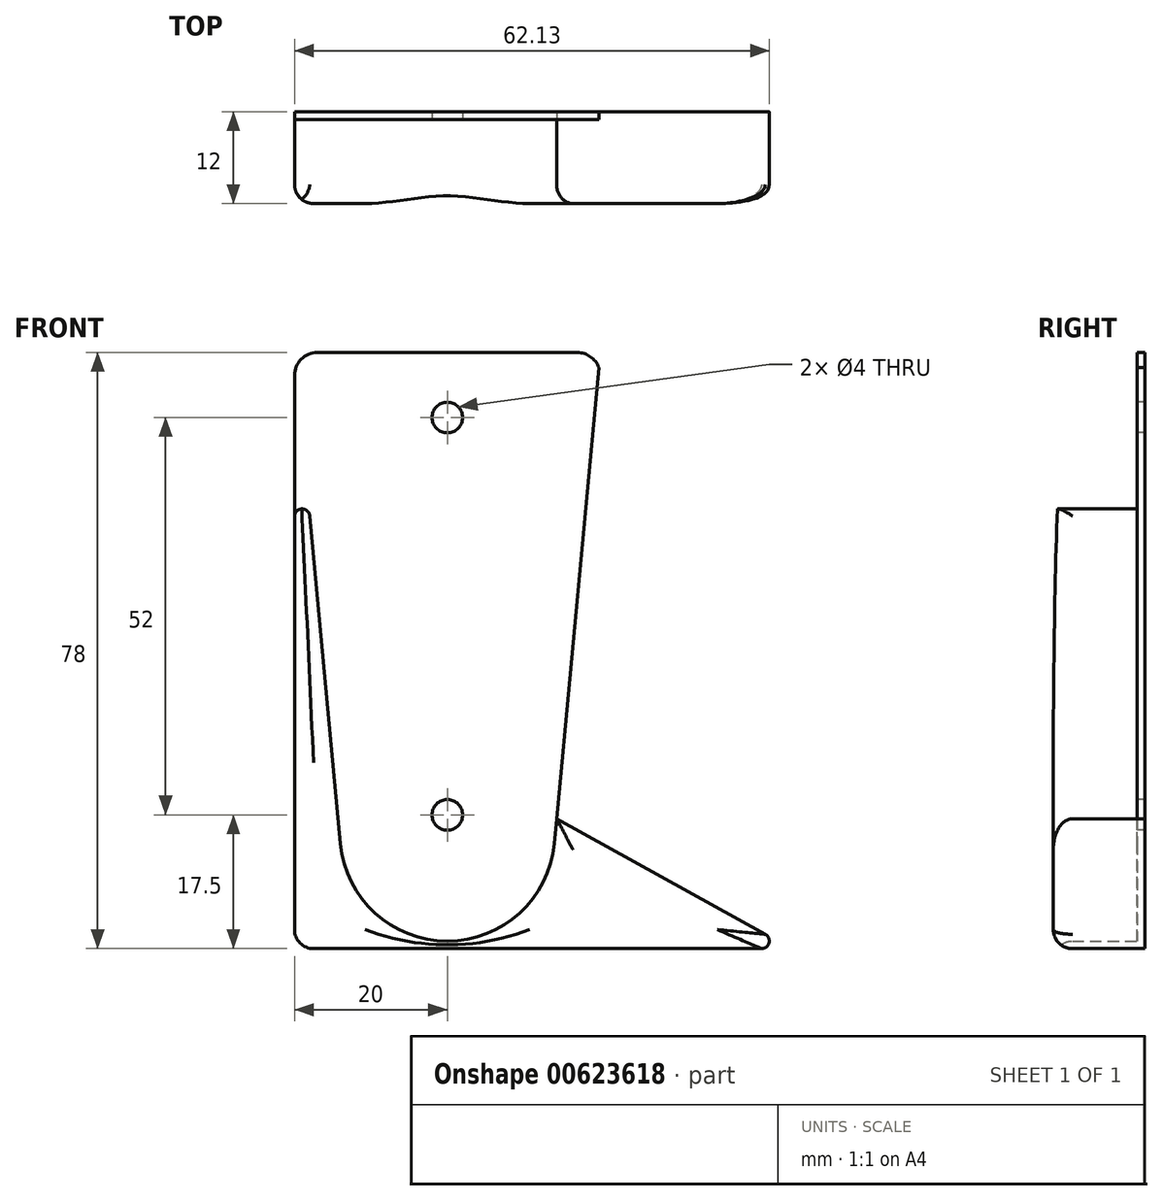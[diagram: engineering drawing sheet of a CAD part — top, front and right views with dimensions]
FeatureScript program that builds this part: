
annotation { "Feature Type Name" : "Feature", "Feature Type Description" : "" }
export const myFeature = defineFeature(function(context is Context, id is Id, definition is map)
    precondition{}
    {
        {
            var Q0;
            Q0=qCreatedBy(makeId("Front.planeOp"),FACE);
            var sketch = newSketch(context, id + "F0", { "sketchPlane" : qUnion([Q0])});
            skLineSegment(sketch, "E0.bottom", {"start": v(-20, 0) * mm, "end": v(20, 0) * mm});
            skLineSegment(sketch, "E0.top", {"start": v(-17, 78) * mm, "end": v(17, 78) * mm});
            skLineSegment(sketch, "E0.left", {"start": v(-20, 0) * mm, "end": v(-20, 75) * mm});
            skLineSegment(sketch, "E0.right", {"start": v(20, 0) * mm, "end": v(20, 75) * mm});
            skLineSegment(sketch, "E1", {"start": v(0, 78) * mm, "end": v(0, 0) * mm, "construction": true});
            skCircle(sketch, "E2", {"center": v(0, 69.5) * mm, "radius": 2 * mm});
            skCircle(sketch, "E3", {"center": v(0, 17.5) * mm, "radius": 2 * mm});
            skLineSegment(sketch, "E4", {"start": v(-12.72, 0) * mm, "end": v(-20, 78) * mm});
            skLineSegment(sketch, "E5", {"start": v(20, 0) * mm, "end": v(45, 0) * mm});
            skLineSegment(sketch, "E6", {"start": v(20, 78) * mm, "end": v(12.72, 0) * mm});
            skArc(sketch, "E7", {"start": v(-14, 13.75) * mm, "mid": v(0, 1) * mm, "end": v(14, 13.75) * mm});
            skLineSegment(sketch, "E8", {"start": v(45, 0) * mm, "end": v(14.3, 17) * mm});
            skPoint(sketch, "E9.visualSharp", {"position": v(20, 78) * mm});
            skArc(sketch, "E9.filletArc", {"start": v(20, 75) * mm, "mid": v(19.12, 77.12) * mm, "end": v(17, 78) * mm});
            skPoint(sketch, "E10.visualSharp", {"position": v(-20, 78) * mm});
            skArc(sketch, "E10.filletArc", {"start": v(-17, 78) * mm, "mid": v(-19.12, 77.12) * mm, "end": v(-20, 75) * mm});
            skSolve(sketch);
        }
        {
            var Q0;
            {var subQ0=sQuery(id+"F0.wireOp",EDGE,"E5");Q0=makeQuery(id+"F0.imprint","IMPRINT",FACE,{"disambiguationData":[TD([[makeQuery(id+"F0.imprint","IMPRINT",EDGE,{"derivedFrom":subQ0}),1.0]])]});}
            var Q1;
            {var subQ0=sQuery(id+"F0.wireOp",EDGE,"E0.left");Q1=makeQuery(id+"F0.imprint","IMPRINT",FACE,{"disambiguationData":[TD([[makeQuery(id+"F0.imprint","IMPRINT",EDGE,{"derivedFrom":subQ0}),-1.0]])]});}
            var Q2;
            {var subQ5=sQuery(id+"F0.wireOp",EDGE,"E7");Q2=makeQuery(id+"F0.imprint","IMPRINT",FACE,{"disambiguationData":[TD([[makeQuery(id+"F0.imprint","IMPRINT",EDGE,{"derivedFrom":subQ5}),-1.0]])]});}
            var Q3;
            {var subQ1=sQuery(id+"F0.wireOp",EDGE,"E0.bottom");var subQ3=sQuery(id+"F0.wireOp",EDGE,"E6");var subQ4=makeQuery(id+"F0.imprint","INTERSECT",VERTEX,{"derivedFrom":[subQ1,subQ3]});Q3=makeQuery(id+"F0.imprint","IMPRINT",FACE,{"disambiguationData":[TD([[makeQuery(id+"F0.imprint","IMPRINT",EDGE,{"disambiguationData":[TD([[subQ4,-1.0]])],"derivedFrom":subQ1}),1.0]])]});}
            var Q4;
            {var subQ1=sQuery(id+"F0.wireOp",EDGE,"E0.top");Q4=makeQuery(id+"F0.imprint","IMPRINT",FACE,{"disambiguationData":[TD([[makeQuery(id+"F0.imprint","IMPRINT",EDGE,{"derivedFrom":subQ1}),-1.0]])]});}
            extrude(context, id + "F1", {"entities" : qUnion([Q0, Q1, Q2, Q3, Q4]), "oppositeDirection" : true, "depth" : 1 * mm, "offsetDistance" : 25 * mm});
        }
        {
            var Q0;
            {var subQ0=sQuery(id+"F0.wireOp",EDGE,"E6");var subQ3=makeQuery(id+"F0.imprint","INTERSECT",VERTEX,{"derivedFrom":[subQ0,sQuery(id+"F0.wireOp",EDGE,"E7")]});Q0=makeQuery(id+"F0.imprint","IMPRINT",FACE,{"disambiguationData":[TD([[makeQuery(id+"F0.imprint","IMPRINT",EDGE,{"disambiguationData":[TD([[subQ3,1.0]])],"derivedFrom":subQ0}),1.0]])]});}
            var Q1;
            {var subQ0=sQuery(id+"F0.wireOp",EDGE,"E5");Q1=makeQuery(id+"F0.imprint","IMPRINT",FACE,{"disambiguationData":[TD([[makeQuery(id+"F0.imprint","IMPRINT",EDGE,{"derivedFrom":subQ0}),1.0]])]});}
            var Q2;
            {var subQ0=sQuery(id+"F0.wireOp",EDGE,"E6");var subQ1=sQuery(id+"F0.wireOp",EDGE,"E0.bottom");var subQ2=makeQuery(id+"F0.imprint","INTERSECT",VERTEX,{"derivedFrom":[subQ1,subQ0]});Q2=makeQuery(id+"F0.imprint","IMPRINT",FACE,{"disambiguationData":[TD([[makeQuery(id+"F0.imprint","IMPRINT",EDGE,{"disambiguationData":[TD([[subQ2,1.0]])],"derivedFrom":subQ1}),1.0]])]});}
            var Q3;
            {var subQ0=sQuery(id+"F0.wireOp",EDGE,"E0.left");Q3=makeQuery(id+"F0.imprint","IMPRINT",FACE,{"disambiguationData":[TD([[makeQuery(id+"F0.imprint","IMPRINT",EDGE,{"derivedFrom":subQ0}),-1.0]])]});}
            var Q4;
            {var subQ0=sQuery(id+"F0.wireOp",EDGE,"E4");var subQ1=sQuery(id+"F0.wireOp",EDGE,"E0.bottom");var subQ2=makeQuery(id+"F0.imprint","INTERSECT",VERTEX,{"derivedFrom":[subQ1,subQ0]});Q4=makeQuery(id+"F0.imprint","IMPRINT",FACE,{"disambiguationData":[TD([[makeQuery(id+"F0.imprint","IMPRINT",EDGE,{"disambiguationData":[TD([[subQ2,-1.0]])],"derivedFrom":subQ1}),1.0]])]});}
            extrude(context, id + "F2", {"entities" : qUnion([Q0, Q1, Q2, Q3, Q4]), "operationType" : NewBodyOperationType.ADD, "depth" : 11 * mm, "offsetDistance" : 25 * mm});
        }
        {
            var Q0;
            Q0=makeQuery(id+"F2.opExtrude","CAP_FACE",FACE,{"disambiguationData":[OSD([sQuery(id+"F0.wireOp",EDGE,"E0.bottom"),sQuery(id+"F0.wireOp",EDGE,"E0.left"),sQuery(id+"F0.wireOp",EDGE,"E4"),sQuery(id+"F0.wireOp",EDGE,"E5"),sQuery(id+"F0.wireOp",EDGE,"E7"),sQuery(id+"F0.wireOp",EDGE,"LuuKxXPf-4tBV-jlHj-Bl1u-vPVHLyxS0asw")])],"isStart":false});
            var Q1;
            {var subQ0=sQuery(id+"F0.wireOp",EDGE,"E0.left");var subQ1=sQuery(id+"F0.wireOp",EDGE,"E0.bottom");Q1=makeQuery(id+"F2.boolean.opBoolean","MERGE",EDGE,{"derivedFrom":[makeQuery(id+"F1.opExtrude","SWEPT_EDGE",EDGE,{"disambiguationData":[OSD([subQ1,subQ0])]}),makeQuery(id+"F2.opExtrude","SWEPT_EDGE",EDGE,{"disambiguationData":[OSD([subQ1,subQ0])]})]});}
            fillet(context, id + "F3", {"entities" : qUnion([Q0, Q1]), "radius" : 2.5 * mm, "tangentPropagation" : true, "allowEdgeOverflow" : false});
        }
        {
            var Q0;
            Q0=makeQuery(id+"F2.opExtrude","SWEPT_EDGE",EDGE,{"disambiguationData":[OSD([sQuery(id+"F0.wireOp",EDGE,"E0.top"),sQuery(id+"F0.wireOp",EDGE,"E0.left"),sQuery(id+"F0.wireOp",EDGE,"E4")])]});
            var Q1;
            {var subQ0=sQuery(id+"F0.wireOp",EDGE,"LuuKxXPf-4tBV-jlHj-Bl1u-vPVHLyxS0asw");var subQ1=sQuery(id+"F0.wireOp",EDGE,"E5");Q1=makeQuery(id+"F2.boolean.opBoolean","MERGE",EDGE,{"derivedFrom":[makeQuery(id+"F1.opExtrude","SWEPT_EDGE",EDGE,{"disambiguationData":[OSD([subQ1,subQ0])]}),makeQuery(id+"F2.opExtrude","SWEPT_EDGE",EDGE,{"disambiguationData":[OSD([subQ1,subQ0])]})]});}
            fillet(context, id + "F4", {"entities" : qUnion([Q0, Q1]), "radius" : 1 * mm, "tangentPropagation" : true, "allowEdgeOverflow" : false});
        }
    });
